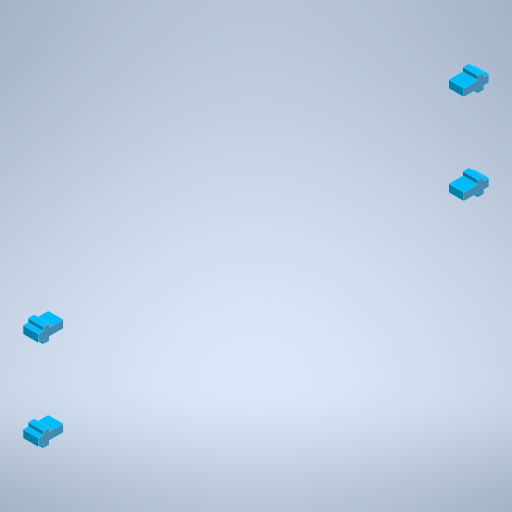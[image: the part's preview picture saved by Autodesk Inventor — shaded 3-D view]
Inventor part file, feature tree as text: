
AUTODESK INVENTOR PART (.ipt)
format: ipt  version: 2024.2 (Build 282272000, 272)  size: 481,792 bytes
history: native  units: mm
features: other x7, extrude x6, sketch x6, reference x2, projected_geometry x1
ambient origin geometry x8: Origin, YZ Plane, XZ Plane, XY Plane, X Axis, Y Axis, Z Axis, Center Point
bodies: Body1 (feature_tree)
feature tree (22):
  other  "Твердое тело1"
  extrude  "Выдавливание1"  Depth=180.0mm
  extrude  "Выдавливание4"  Depth=84.0mm
  extrude  "Выдавливание5"  Depth=90.0mm
  extrude  "Выдавливание7"  TaperAngle=0.0deg  [1 undecoded]
  extrude  "Выдавливание8"  Depth=6.0mm
  extrude  "Выдавливание9"  Depth=8.0mm
  sketch  "Эскиз1"
  sketch  "Эскиз4"
  sketch  "Эскиз6"
  sketch  "Эскиз8"
  sketch  "Эскиз9"
  reference  "Ссылка1"
  reference  "Ссылка2"
  sketch  "Эскиз10"
  projected_geometry  "Спроецированная петля1"
  other  "<userpath>\Documents\Artist\3D\Робот.iam"
  other  "Робот.iam"
  other  "каретка:1"
  other  "ANY:13"
  other  "Проецирование ребер1"
  other  "Проецирование ребер2"
note: 1 required parameter value undecoded (feature->parameter linkage not recoverable at this tier; creation-order binding heuristic only, values carry confidence <= 0.55)
